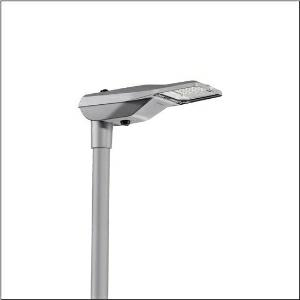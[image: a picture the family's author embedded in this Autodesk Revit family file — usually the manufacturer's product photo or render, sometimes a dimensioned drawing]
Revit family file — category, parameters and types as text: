
# Revit family: streetlight_sl_21_iq_micro___stw1_0a_5xe1e31y08db_aea3
name_source: partatom
category: Lighting Fixtures
units: mm (PartAtom-declared; Revit-internal decimal feet)

## family parameters
Cut with Voids When Loaded = No
Host = Face
Light Source = No
Part Type = Normal
Room Calculation Point = No
Round Connector Dimension = Use Diameter
Shared = No

## types (1)
- --- (1 x LED, 5110 lm, 39.1 W, 3000K)
    Apparent Load = 39 VA
    CIE Flux Codes = 38 75 98 100 100
    Color Rendering = 70
    Color Temperature = 3000K
    Default Elevation = 1800 mm
    Description = Streetlight SL 21 iQ micro, mast luminaire, primary light control with lens, of PMMA, primary optical cover: cover, of toughened safety glass, transparent, light distribution: STW1.0a, light emission: direct distribution, primary light characteristic: asymmetric, installation type: post-top, side-entry, LED, High Power LED, rated luminous flux: 5.110lm, luminous efficacy: 131lm/W, light colour: 730, colour temperature: 3000K, control gear: iQ-Street Remote, D4i with power reduction, control: pre-setting: logarithmic dimming characteristic, Street-Remote, Auto-Match, Temp-Guard, Lumen-Switch, Night-Set, Smart-Wire, Light-Fading, Desk-Remote (wireless, voltage-free reading and setting of iQ features in the workshop via application-optimized NFC function/RFID function), optimised constant luminous flux control (CLO 2.0), mains connection: 220..240V, AC, 50/60Hz, start of lifetime: 39W, end of service life: 41W, reduction: 17W, luminaire housing, of diecast aluminium, powder-coated, Siteco® metallic grey (DB 702S), corrosivity category C5 mid according to DIN EN ISO 12944, please order mast flange separately, inclination adjustable: 0°, 5°, 10°, 15°, sealing non-destructively replaceable, multi-level sealing system, length: 528mm, width: 235mm, height: 110mm, mast flange for spigot size: 42mm (side-entry): 5XC10008XM4, 60/48mm (side-entry/post-top): 5XC10108XM2, 76/60mm (side-entry/post-top): 5XC10108XM1, mounting height: 4..8m, Smart Interface below and above, protection rating (complete): IP66, insulation class (complete): insulation class II (safety insulation), certification: CE, ENEC, ENEC+, VDE, impact resistance: IK10, permissible operating ambient temperature for outdoor applications: -40..+50°C, standard-compliant lighting for roads and squares, packaging unit: 1 piece

Light Distribution: STW1.0a
    Height = 110 mm
    Lamp = 1 x LED
    Lamp Light Flux = 5110 lm
    Lamp Power = 39.1 W
    Lamp count = 1
    Length = 528 mm
    Luminous efficacy = 131 lm/W
    Manufacturer = Siteco
    ModVariant = No
    Model = 5XE1E31Y08DB
    Number of Poles = 1
    OnlyDefault = Yes
    Power Factor = 1
    Product Name = Streetlight SL 21 iQ micro | STW1.0a
    Product group = mast luminaire | pylon top
    ProductGroupID = 6100
    Protection Class = Protection class II
    Protection Degree = IP 66
    RLX_Detail_Level = 1
    RLX_Emergency_Light_Flux = 0 lm
    RLX_Emergency_Type = 0
    RLX_Emergency_Type_DB = No
    RlxData = <blob elided: 98625 chars, md5=ed9e7e5b>
    Socket = socket
    Standby Power = 0 W
    System Light Flux = 5110 lm
    System Power = 39 W
    Type Comments = factory setting: luminous flux: 100 % | dim-lin: 254 | 765 mA
    Type Image = l_1007239.jpg
    URL = http://relux.com
    VarID = @adj_135855
    Voltage = 0 V
    Weight = 0.00 kg
    Width = 235 mm

## geometry (parser evidence)
native form markers: Blend x4, Sweep x10
no freeform markers — native parametric forms only
